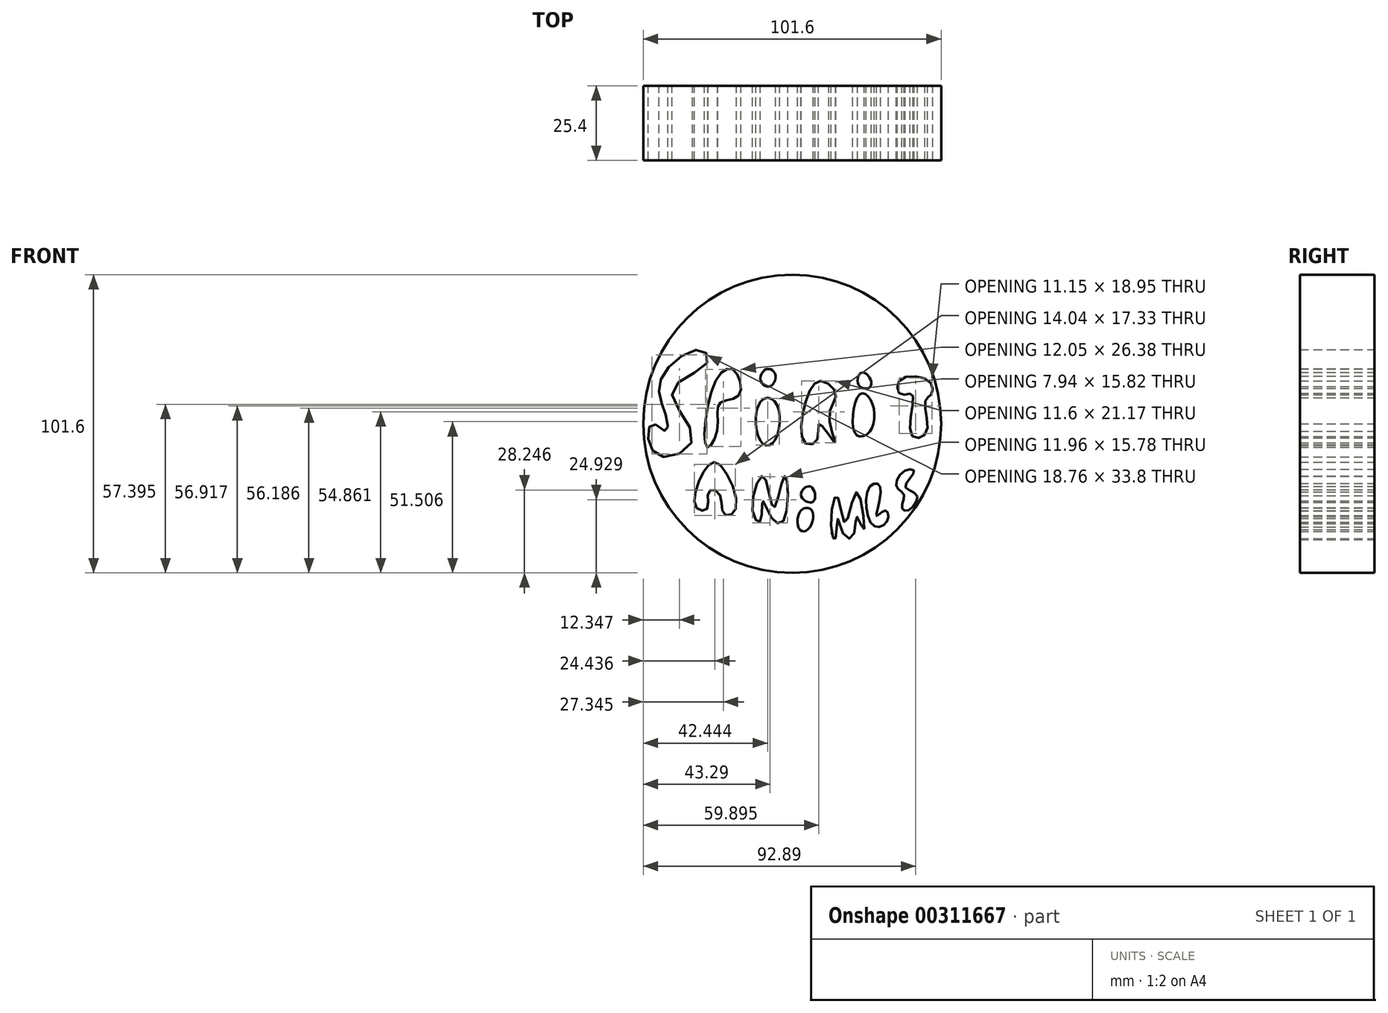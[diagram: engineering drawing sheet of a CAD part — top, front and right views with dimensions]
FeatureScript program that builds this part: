
annotation { "Feature Type Name" : "Feature", "Feature Type Description" : "" }
export const myFeature = defineFeature(function(context is Context, id is Id, definition is map)
    precondition{}
    {
        {
            var Q0;
            Q0=qCreatedBy(makeId("Front.planeOp"),FACE);
            var sketch = newSketch(context, id + "F0", { "sketchPlane" : qUnion([Q0])});
            skCircle(sketch, "E0", {"center": v(0, 0) * mm, "radius": 50.8 * mm});
            skSolve(sketch);
        }
        {
            var Q0;
            Q0 = qSketchRegion(id + "F0", true);
            extrude(context, id + "F1", {"entities" : qUnion([Q0]), "depth" : 25.4 * mm});
        }
        {
            var Q0;
            Q0=qCreatedBy(makeId("Front.planeOp"),FACE);
            var sketch = newSketch(context, id + "F2", { "sketchPlane" : qUnion([Q0])});
            skFitSpline(sketch, "E1", {"points": [v(-29.07, 20.7) * mm, v(-40.94, 11.16) * mm, v(-33.96, -4.88) * mm, v(-44.42, -11.16) * mm, v(-49.08, -4.65) * mm, v(-47.45, 0) * mm, v(-43.03, -2.56) * mm, v(-42.8, 1.86) * mm, v(-45.35, 10.23) * mm, v(-42.33, 19.07) * mm, v(-30.93, 25.12) * mm, v(-29.07, 20.7) * mm]});
            skFitSpline(sketch, "E2", {"points": [v(-26.05, 14.65) * mm, v(-29.07, -7.9) * mm, v(-25.58, -2.1) * mm, v(-24.65, 6.98) * mm, v(-18.14, 9.77) * mm, v(-19.77, 18.14) * mm, v(-26.05, 14.65) * mm]});
            skFitSpline(sketch, "E3", {"points": [v(-10.7, 7.68) * mm, v(-10.7, -6.05) * mm, v(-6.28, -6.28) * mm, v(-5.58, 7.21) * mm, v(-10.7, 7.68) * mm]});
            skFitSpline(sketch, "E4", {"points": [v(-8.84, 18.6) * mm, v(-10.7, 14.65) * mm, v(-7.44, 12.8) * mm, v(-5.81, 16.98) * mm, v(-8.84, 18.6) * mm]});
            skFitSpline(sketch, "E5", {"points": [v(4.65, 7.68) * mm, v(4.42, -6.51) * mm, v(8.6, -5.35) * mm, v(9.3, 0) * mm, v(14.65, -6.51) * mm, v(12.56, 2.8) * mm, v(14.89, 10) * mm, v(9.77, 14.65) * mm, v(4.65, 7.68) * mm]});
            skFitSpline(sketch, "E6", {"points": [v(23.03, 10) * mm, v(21.63, -3.49) * mm, v(26.51, -2.56) * mm, v(26.98, 7.68) * mm, v(23.03, 10) * mm]});
            skFitSpline(sketch, "E7", {"points": [v(25.35, 16.98) * mm, v(23.03, 16.98) * mm, v(23.03, 12.8) * mm, v(26.75, 12.8) * mm, v(25.35, 16.98) * mm]});
            skFitSpline(sketch, "E8", {"points": [v(36.52, 14.65) * mm, v(37.21, 10) * mm, v(40.94, 10) * mm, v(40.7, -3.72) * mm, v(45.59, -3.26) * mm, v(45.35, 7.68) * mm, v(47.45, 10) * mm, v(46.52, 14.65) * mm, v(36.52, 14.65) * mm]});
            skFitSpline(sketch, "E9", {"points": [v(-30.24, -16.51) * mm, v(-32.8, -28.38) * mm, v(-29.07, -29.07) * mm, v(-28.38, -23.03) * mm, v(-24.89, -23.72) * mm, v(-23.26, -30.7) * mm, v(-19.3, -29.3) * mm, v(-25.35, -13.5) * mm, v(-30.24, -16.51) * mm]});
            skFitSpline(sketch, "E10", {"points": [v(-13.5, -29.54) * mm, v(-9.77, -17.9) * mm, v(-6.28, -28.6) * mm, v(-2.56, -17.9) * mm, v(-2.56, -32.33) * mm, v(-6.28, -33.03) * mm, v(-10, -26.28) * mm, v(-10.93, -33.26) * mm, v(-13.5, -29.54) * mm]});
            skFitSpline(sketch, "E11", {"points": [v(3.02, -29.54) * mm, v(2.56, -36.05) * mm, v(5.58, -35.82) * mm, v(6.75, -29.54) * mm, v(3.02, -29.54) * mm]});
            skFitSpline(sketch, "E12", {"points": [v(6.28, -21.4) * mm, v(3.02, -24.42) * mm, v(7.21, -26.51) * mm, v(6.28, -21.4) * mm]});
            skFitSpline(sketch, "E13", {"points": [v(13.26, -34.66) * mm, v(15.35, -24.65) * mm, v(18.14, -33.73) * mm, v(22.1, -23.26) * mm, v(24.42, -36.05) * mm, v(22.1, -31.63) * mm, v(20.7, -38.38) * mm, v(17.68, -37.91) * mm, v(15.58, -32.33) * mm, v(14.65, -39.3) * mm, v(13.26, -34.66) * mm]});
            skFitSpline(sketch, "E14", {"points": [v(26.51, -21.4) * mm, v(27.68, -34.66) * mm, v(32.56, -32.8) * mm, v(31.63, -29.54) * mm, v(28.84, -31.4) * mm, v(30, -21.4) * mm, v(26.51, -21.4) * mm]});
            skFitSpline(sketch, "E15", {"points": [v(38.38, -16.05) * mm, v(35.59, -21.4) * mm, v(38.14, -24.19) * mm, v(37.45, -28.6) * mm, v(39.54, -29.54) * mm, v(42.56, -24.42) * mm, v(38.6, -21.4) * mm, v(41.63, -16.28) * mm, v(38.38, -16.05) * mm]});
            skSolve(sketch);
        }
        {
            var Q0;
            Q0 = qSketchRegion(id + "F2", true);
            extrude(context, id + "F3", {"entities" : qUnion([Q0]), "operationType" : NewBodyOperationType.REMOVE, "endBound" : BoundingType.SYMMETRIC, "oppositeDirection" : true, "depth" : 50.8 * mm});
        }
    });
